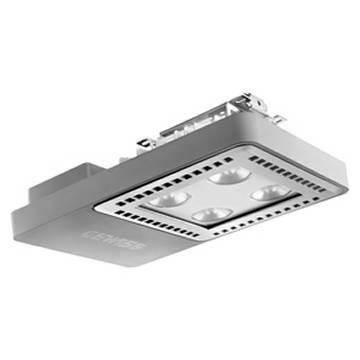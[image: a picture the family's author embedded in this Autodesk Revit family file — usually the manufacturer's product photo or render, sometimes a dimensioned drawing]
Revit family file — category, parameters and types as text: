
# Revit family: Lighting-Industrial-GEWISS-SMART[4]HLO_HIGHBAYS-LED_1M_DALI
name_source: partatom
category: Apparecchi per illuminazione
units: mm (PartAtom-declared; Revit-internal decimal feet)

## family parameters
Basato su piano di lavoro = Sì
Condiviso = No
Numero OmniClass = 23.80.00.00
Punto di calcolo locali = No
Quota connettore circolare = Usa diametro
Sempre verticale = No
Sorgente d'illuminazione = No
Taglio con vuoti quando caricato = No
Tipo di parte = Normale
Titolo OmniClass = Electric Power and Lighting

## types (36) — shared parameters
Application = Internal
Body = PA6 "Halogen Free" loaded fibreglass
Carico apparente = 50 VA
Catalogue = LIGHTING
Classification: = -
Classificazione = Lighting
Color Rendering Index = CRI-80
Colour = Grey RAL 7035
Colour : = Grey RAL 7035
Commenti sul wattaggio = 50W
Context = Logistics and industrial manufacturing lighting
Control System = 1 x DALI DT6
Control System : = DALI
DIN 18032-3 certification = With Bracket - Rope Kit + terminal&nbsp;(in approval)
Device with reduced surface temperature = Yes
Distanza tot_plafoniera = 74 mm  [stored 0.242782 ft]
Driver = Included
Driver Box = Built-in
Electrocod = 2444
Eletrical and lighting features = -
External screw = Stainless steel
Fixing = -
Gasket = anti-aging silicone
General information = -
Glow Wire Test : = 850 °C
IDF = f2ed7942-e2f7-4533-ac64-b961166995a0
IDT = 0f19f0c5244441bab192072dc14552b5
IP degree = IP66
IPEA = -
Immagine tipo = GWL1071.jpg
Installationa and maintenance = -
Insulation class = I
LED Maintenance = Non-replaceable
Lampada = LED
Larghezza = 253 mm  [stored 0.830052 ft]
Lifetime = L90B10 (Tq+25°C) = 100.000 h - L90B10 (Tq+50°C) = 50.000 h
Locking Hook = -
Luminaire = LED Industrial ReflectorÂ
Lunghezza = 383 mm  [stored 1.25656 ft]
Materials = -
Maximum surface exposed to the wind : = 0,097 m²
Motore = <Per categoria>
Mouting and installation = Ceiling - Wallmounting - Suspension
Operating temperature : = -30°C ÷ +50 °C
Optic Maintenance = Non-replaceable
Optic and illuminating features = -
Overvoltage protection = DM 6 kV / CM 10 kV
Photobiological Risk Class = RG0
Plafoniera = <Per categoria>
Produttore = GEWISS S.p.A.
Prospetto di default = 1219 mm
Raggio led = 30 mm  [stored 0.0984252 ft]
Rated frequency (Hz) = 50/60 Hz
Shield type = Tempered glass Thickness 4mm
Shock resistance = IK08
Spessore plafoniera = 40 mm  [stored 0.131234 ft]
Standard Deviation Colour Matching = SDCM = 3
Standard- = EN 60598-1 ; EN 60598-2-1 ; EN 60598-2-24
Standards and approvals = -
Stocking temperature = -40 +70 °C
Supply voltage = 220 - 240 V
System power = 64W
Technical sheet = https://www.gewiss.com
Tilt- = With bracket accessory
Trasformatore = <Per categoria>
Type of light source = LED - Not replaceable
URL = https://www.gewiss.com
Unique digital code (Datamatrix) = Datamatrix
Version file RFA = 20.11
Vetro acceso = Lampada accesa
Voltaggio = 230 V
Warranty = 5 years
Weight (kg): = 3,5
Wiring = With GW connect watertight connector

## per-type parameters (varying)
| type | Colour temperature | Descrizione | Efficiency (lm/W) | Lumen output (lm) | Modello | Optic | Optic : | SEO | Unified Glare Rating |
| GWS4123BP840 - SMART4LB 1M C.PAS.DALI HLO 90° 40K | 4000K | SMART[4]LB 1M C.PAS.DALI HLO 90° 40K | 144 | 9200 | GWS4123BP840 | 90° | Metallic PC reflector and PMMA lenses |  | UGR - 25 |
| GWS4123BF840 - SMART4LB 1M C.PAS.DALI HLO 30° 40K | 4000K | SMART[4]LB 1M C.PAS.DALI HLO 30° 40K | 141 | 9000 | GWS4123BF840 | 30° | Metallic PC reflector and PMMA lenses |  | UGR - 22 |
| GWS4123BA830 - SMART4LB 1M C.PAS.DALI HLO ARR.30K | 3000K | SMART[4]LB 1M C.PAS.DALI HLO ARR.30K | 136 | 8700 | GWS4123BA830 | Array | Metallized polycarbonate reflector |  | - |
| GWS4121BF857 - SMART4LB 1M ST.AL.DALI HLO 30° 57K | 5700K | SMART[4]LB 1M ST.AL.DALI HLO 30° 57K | 141 | 9000 | GWS4121BF857 | 30° | Metallic PC reflector and PMMA lenses |  | UGR - 22 |
| GWS4121BP840 - SMART4LB 1M ST.AL.DALI HLO 90° 40K | 4000K | SMART[4]LB 1M ST.AL.DALI HLO 90° 40K | 144 | 9200 | GWS4121BP840 | 90° | Metallic PC reflector and PMMA lenses |  | UGR - 25 |
| GWS4123BC840 - SMART4LB 1M C.PAS.DALI HLO ASI.40K | 4000K | SMART[4]LB 1M C.PAS.DALI HLO ASI.40K | 128 | 8200 | GWS4123BC840 | Asymmetrical | Metallic PC reflector and PMMA lenses | Low bay | - |
| GWS4123BP830 - SMART4LB 1M C.PAS.DALI HLO 90° 30K | 3000K | SMART[4]LB 1M C.PAS.DALI HLO 90° 30K | 138 | 8800 | GWS4123BP830 | 90° | Metallic PC reflector and PMMA lenses |  | UGR - 25 |
| GWS4121BP830 - SMART4LB 1M ST.AL.DALI HLO 90° 30K | 3000K | SMART[4]LB 1M ST.AL.DALI HLO 90° 30K | 138 | 8800 | GWS4121BP830 | 90° | Metallic PC reflector and PMMA lenses |  | UGR - 25 |
| GWS4123BC830 - SMART4LB 1M C.PAS.DALI HLO ASI.30K | 3000K | SMART[4]LB 1M C.PAS.DALI HLO ASI.30K | 122 | 7800 | GWS4123BC830 | Asymmetrical | Metallic PC reflector and PMMA lenses | Low bay | - |
| GWS4121BH857 - SMART4LB 1M ST.AL.DALI HLO 60° 57K | 5700K | SMART[4]LB 1M ST.AL.DALI HLO 60° 57K | 144 | 9200 | GWS4121BH857 | 60° | Metallic PC reflector and PMMA lenses |  | UGR - 25 |
| GWS4121BC840 - SMART4LB 1M ST.AL.DALI HLO ASI.40K | 4000K | SMART[4]LB 1M ST.AL.DALI HLO ASI.40K | 128 | 8200 | GWS4121BC840 | Asymmetrical | Metallic PC reflector and PMMA lenses | Low bay | - |
| GWS4123BH857 - SMART4LB 1M C.PAS.DALI HLO 60° 57K | 5700K | SMART[4]LB 1M C.PAS.DALI HLO 60° 57K | 144 | 9200 | GWS4123BH857 | 60° | Metallic PC reflector and PMMA lenses |  | UGR - 25 |
| GWS4121BC830 - SMART4LB 1M ST.AL.DALI HLO ASI.30K | 3000K | SMART[4]LB 1M ST.AL.DALI HLO ASI.30K | 122 | 7800 | GWS4121BC830 | Asymmetrical | Metallic PC reflector and PMMA lenses | Low bay | - |
| GWS4123BH830 - SMART4LB 1M C.PAS.DALI HLO 60° 30K | 3000K | SMART[4]LB 1M C.PAS.DALI HLO 60° 30K | 136 | 8700 | GWS4123BH830 | 60° | Metallic PC reflector and PMMA lenses |  | UGR - 25 |
| GWS4123BP857 - SMART4LB 1M C.PAS.DALI HLO 90° 57K | 5700K | SMART[4]LB 1M C.PAS.DALI HLO 90° 57K | 144 | 9200 | GWS4123BP857 | 90° | Metallic PC reflector and PMMA lenses |  | UGR - 25 |
| GWS4123BQ840 - SMART4LB 1M C.PAS.DALI HLO ELL.40K | 4000K | SMART[4]LB 1M C.PAS.DALI HLO ELL.40K | 128 | 8200 | GWS4123BQ840 | Elliptical | Metallic PC reflector and PMMA lenses | Low bay | - |
| GWS4121BF840 - SMART4LB 1M ST.AL.DALI HLO 30° 40K | 4000K | SMART[4]LB 1M ST.AL.DALI HLO 30° 40K | 141 | 9000 | GWS4121BF840 | 30° | Metallic PC reflector and PMMA lenses |  | UGR - 22 |
| GWS4123BA857 - SMART4LB 1M C.PAS.DALI HLO ARR.57K | 5700K | SMART[4]LB 1M C.PAS.DALI HLO ARR.57K | 144 | 9200 | GWS4123BA857 | Array | Metallized polycarbonate reflector |  | - |
| GWS4121BH840 - SMART4LB 1M ST.AL.DALI HLO 60° 40K | 4000K | SMART[4]LB 1M ST.AL.DALI HLO 60° 40K | 144 | 9200 | GWS4121BH840 | 60° | Metallic PC reflector and PMMA lenses |  | UGR - 25 |
| GWS4123BH840 - SMART4LB 1M C.PAS.DALI HLO 60° 40K | 4000K | SMART[4]LB 1M C.PAS.DALI HLO 60° 40K | 144 | 9200 | GWS4123BH840 | 60° | Metallic PC reflector and PMMA lenses |  | UGR - 25 |
| GWS4123BQ830 - SMART4LB 1M C.PAS.DALI HLO ELL.30K | 3000K | SMART[4]LB 1M C.PAS.DALI HLO ELL.30K | 122 | 7800 | GWS4123BQ830 | Elliptical | Metallic PC reflector and PMMA lenses | Low bay | - |
| GWS4121BQ830 - SMART4LB 1M ST.AL.DALI HLO ELL.30K | 3000K | SMART[4]LB 1M ST.AL.DALI HLO ELL.30K | 122 | 7800 | GWS4121BQ830 | Elliptical | Metallic PC reflector and PMMA lenses | Low bay | - |
| GWS4123BQ857 - SMART4LB 1M C.PAS.DALI HLO ELL.57K | 5700K | SMART[4]LB 1M C.PAS.DALI HLO ELL.57K | 128 | 8200 | GWS4123BQ857 | Elliptical | Metallic PC reflector and PMMA lenses | Low bay | - |
| GWS4121BA830 - SMART4LB 1M ST.AL.DALI HLO ARR.30K | 3000K | SMART[4]LB 1M ST.AL.DALI HLO ARR.30K | 136 | 8700 | GWS4121BA830 | Array | Metallized polycarbonate reflector |  | - |
| GWS4121BQ840 - SMART4LB 1M ST.AL.DALI HLO ELL.40K | 4000K | SMART[4]LB 1M ST.AL.DALI HLO ELL.40K | 128 | 8200 | GWS4121BQ840 | Elliptical | Metallic PC reflector and PMMA lenses | Low bay | - |
| GWS4121BA857 - SMART4LB 1M ST.AL.DALI HLO ARR.57K | 5700K | SMART[4]LB 1M ST.AL.DALI HLO ARR.57K | 144 | 9200 | GWS4121BA857 | Array | Metallized polycarbonate reflector |  | - |
| GWS4121BA840 - SMART4LB 1M ST.AL.DALI HLO ARR.40K | 4000K | SMART[4]LB 1M ST.AL.DALI HLO ARR.40K | 144 | 9200 | GWS4121BA840 | Array | Metallized polycarbonate reflector |  | - |
| GWS4123BA840 - SMART4LB 1M C.PAS.DALI HLO ARR.40K | 4000K | SMART[4]LB 1M C.PAS.DALI HLO ARR.40K | 144 | 9200 | GWS4123BA840 | Array | Metallized polycarbonate reflector |  | - |
| GWS4121BH830 - SMART4LB 1M ST.AL.DALI HLO 60° 30K | 3000K | SMART[4]LB 1M ST.AL.DALI HLO 60° 30K | 136 | 8700 | GWS4121BH830 | 60° | Metallic PC reflector and PMMA lenses |  | UGR - 25 |
| GWS4123BF830 - SMART4LB 1M C.PAS.DALI HLO 30° 30K | 3000K | SMART[4]LB 1M C.PAS.DALI HLO 30° 30K | 134 | 8600 | GWS4123BF830 | 30° | Metallic PC reflector and PMMA lenses |  | UGR - 22 |
| GWS4121BF830 - SMART4LB 1M ST.AL.DALI HLO 30° 30K | 3000K | SMART[4]LB 1M ST.AL.DALI HLO 30° 30K | 134 | 8600 | GWS4121BF830 | 30° | Metallic PC reflector and PMMA lenses |  | UGR - 22 |
| GWS4121BC857 - SMART4LB 1M ST.AL.DALI HLO ASI.57K | 5700K | SMART[4]LB 1M ST.AL.DALI HLO ASI.57K | 128 | 8200 | GWS4121BC857 | Asymmetrical | Metallic PC reflector and PMMA lenses | Low bay | - |
| GWS4121BQ857 - SMART4LB 1M ST.AL.DALI HLO ELL.57K | 5700K | SMART[4]LB 1M ST.AL.DALI HLO ELL.57K | 128 | 8200 | GWS4121BQ857 | Elliptical | Metallic PC reflector and PMMA lenses | Low bay | - |
| GWS4123BF857 - SMART4LB 1M C.PAS.DALI HLO 30° 57K | 5700K | SMART[4]LB 1M C.PAS.DALI HLO 30° 57K | 141 | 9000 | GWS4123BF857 | 30° | Metallic PC reflector and PMMA lenses |  | UGR - 22 |
| GWS4121BP857 - SMART4LB 1M ST.AL.DALI HLO 90° 57K | 5700K | SMART[4]LB 1M ST.AL.DALI HLO 90° 57K | 144 | 9200 | GWS4121BP857 | 90° | Metallic PC reflector and PMMA lenses |  | UGR - 25 |
| GWS4123BC857 - SMART4LB 1M C.PAS.DALI HLO ASI.57K | 5700K | SMART[4]LB 1M C.PAS.DALI HLO ASI.57K | 128 | 8200 | GWS4123BC857 | Asymmetrical | Metallic PC reflector and PMMA lenses | Low bay | - |

note: [stored X ft] marks values corroborated as IEEE doubles in the binary element streams (Revit-internal decimal feet)

## geometry (parser evidence)
native form markers: Blend x4
no freeform markers — native parametric forms only
